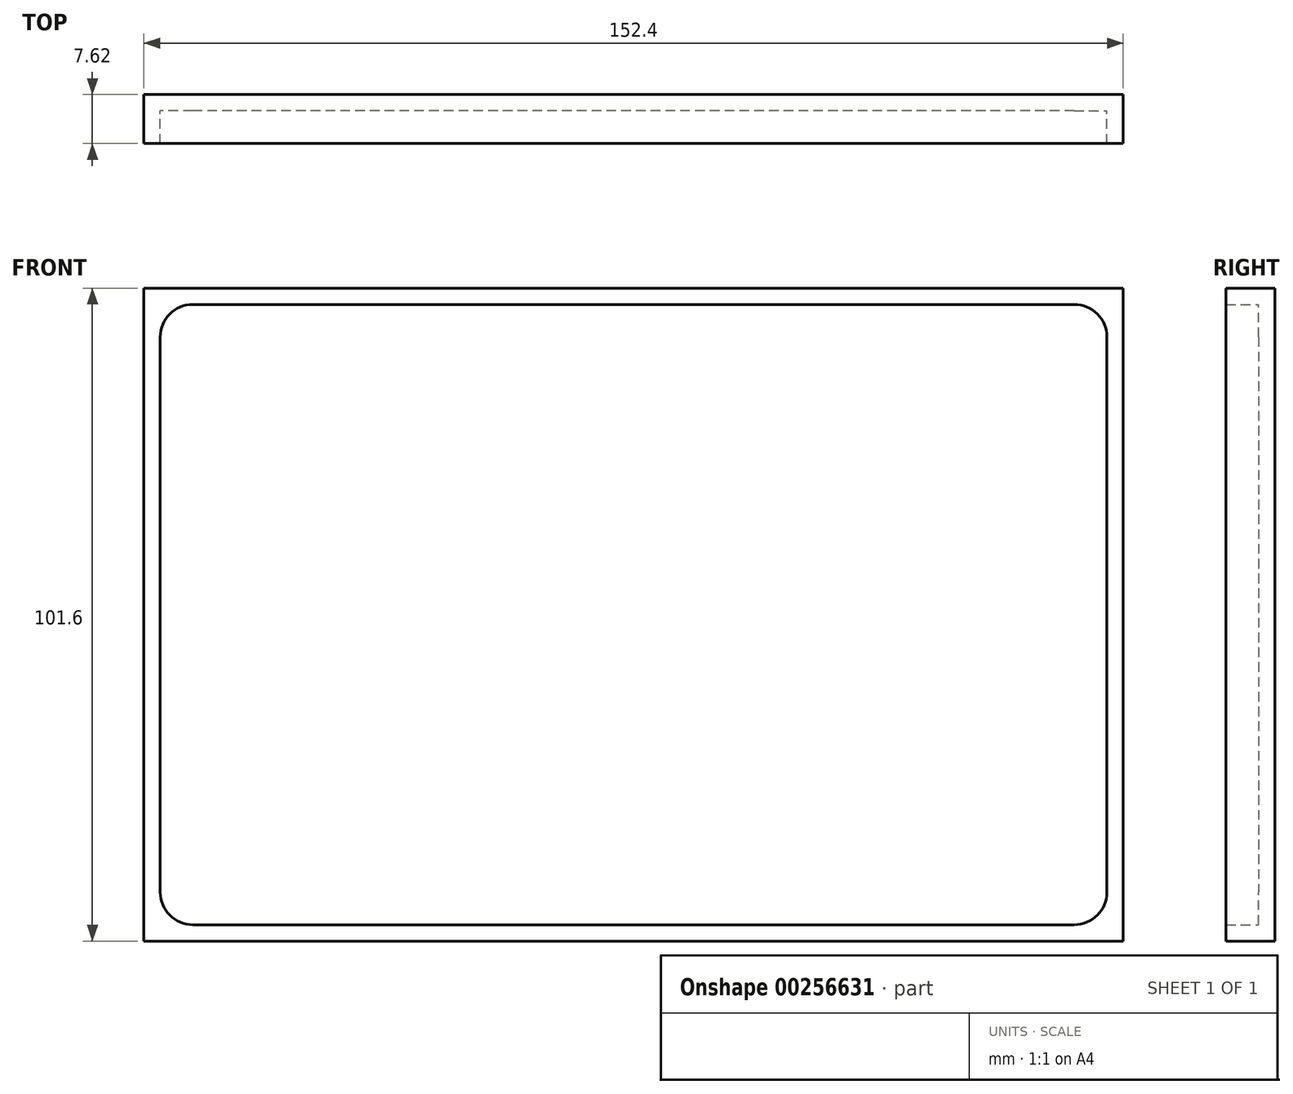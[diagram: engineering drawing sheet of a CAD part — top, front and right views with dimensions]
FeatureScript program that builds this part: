
annotation { "Feature Type Name" : "Feature", "Feature Type Description" : "" }
export const myFeature = defineFeature(function(context is Context, id is Id, definition is map)
    precondition{}
    {
        {
            var Q0;
            Q0=qCreatedBy(makeId("Front.planeOp"),FACE);
            var sketch = newSketch(context, id + "F0", { "sketchPlane" : qUnion([Q0])});
            skLineSegment(sketch, "E0.bottom", {"start": v(76.2, 50.8) * mm, "end": v(-76.2, 50.8) * mm});
            skLineSegment(sketch, "E0.top", {"start": v(76.2, -50.8) * mm, "end": v(-76.2, -50.8) * mm});
            skLineSegment(sketch, "E0.left", {"start": v(76.2, 50.8) * mm, "end": v(76.2, -50.8) * mm});
            skLineSegment(sketch, "E0.right", {"start": v(-76.2, 50.8) * mm, "end": v(-76.2, -50.8) * mm});
            skPoint(sketch, "E0.middle", {"position": v(0, 0) * mm});
            skSolve(sketch);
        }
        {
            var Q0;
            Q0=makeQuery(id+"F0.imprint","IMPRINT",FACE,{"disambiguationData":[TD([[makeQuery(id+"F0.imprint","IMPRINT",EDGE,{"derivedFrom":sQuery(id+"F0.wireOp",EDGE,"E0.bottom")}),1.0]])]});
            extrude(context, id + "F1", {"entities" : qUnion([Q0]), "depth" : 7.62 * mm});
        }
        {
            var Q0;
            Q0=makeQuery(id+"F1.opExtrude","CAP_FACE",FACE,{"disambiguationData":[OSD([sQuery(id+"F0.wireOp",EDGE,"E0.bottom"),sQuery(id+"F0.wireOp",EDGE,"E0.top"),sQuery(id+"F0.wireOp",EDGE,"E0.left"),sQuery(id+"F0.wireOp",EDGE,"E0.right")])],"isStart":false});
            shell(context, id + "F2", {"entities" : qUnion([Q0]), "thickness" : 2.54 * mm});
        }
        {
            var Q0;
            Q0=makeQuery(id+"F2.opShell","OFFSET_EDGE",EDGE,{"disambiguationData":[OSD([sQuery(id+"F0.wireOp",EDGE,"E0.bottom"),sQuery(id+"F0.wireOp",EDGE,"E0.right")])]});
            var Q1;
            Q1=makeQuery(id+"F2.opShell","OFFSET_EDGE",EDGE,{"disambiguationData":[OSD([sQuery(id+"F0.wireOp",EDGE,"E0.top"),sQuery(id+"F0.wireOp",EDGE,"E0.right")])]});
            var Q2;
            Q2=makeQuery(id+"F2.opShell","OFFSET_EDGE",EDGE,{"disambiguationData":[OSD([sQuery(id+"F0.wireOp",EDGE,"E0.bottom"),sQuery(id+"F0.wireOp",EDGE,"E0.left")])]});
            var Q3;
            Q3=makeQuery(id+"F2.opShell","OFFSET_EDGE",EDGE,{"disambiguationData":[OSD([sQuery(id+"F0.wireOp",EDGE,"E0.top"),sQuery(id+"F0.wireOp",EDGE,"E0.left")])]});
            fillet(context, id + "F3", {"entities" : qUnion([Q0, Q1, Q2, Q3]), "radius" : 5.08 * mm, "tangentPropagation" : true, "allowEdgeOverflow" : false});
        }
    });
